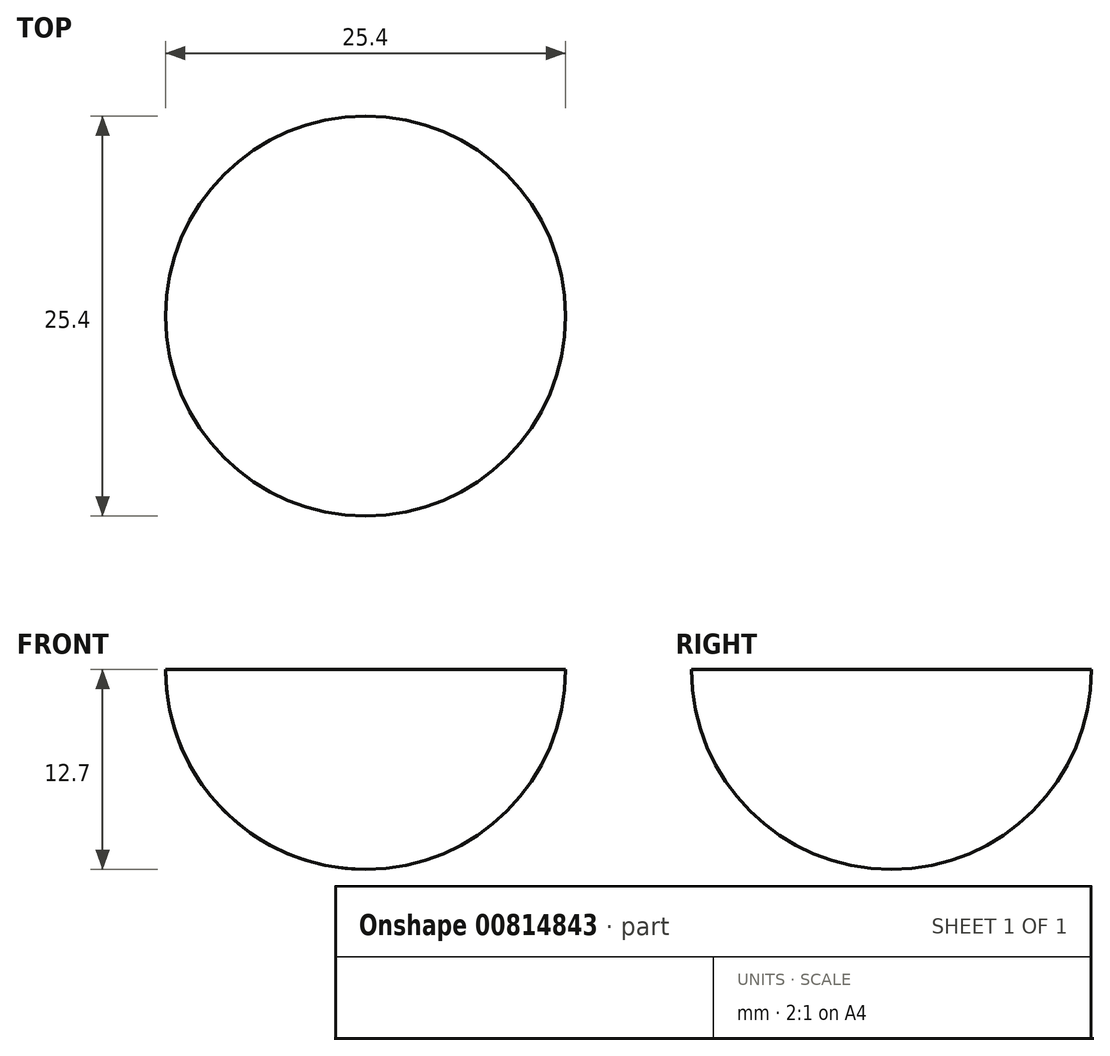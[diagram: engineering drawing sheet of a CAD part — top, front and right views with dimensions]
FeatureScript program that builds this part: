
annotation { "Feature Type Name" : "Feature", "Feature Type Description" : "" }
export const myFeature = defineFeature(function(context is Context, id is Id, definition is map)
    precondition{}
    {
        {
            var Q0;
            Q0=qCreatedBy(makeId("Front.planeOp"),FACE);
            var sketch = newSketch(context, id + "F0", { "sketchPlane" : qUnion([Q0])});
            skArc(sketch, "E0", {"start": v(0, -12.7) * mm, "mid": v(12.7, 0) * mm, "end": v(0, 12.7) * mm});
            skLineSegment(sketch, "E1", {"start": v(0, -12.7) * mm, "end": v(0, 12.7) * mm});
            skSolve(sketch);
        }
        {
            var Q0;
            Q0 = qSketchRegion(id + "F0", true);
            var Q1;
            Q1=sQuery(id+"F0.wireOp",EDGE,"E1");
            revolve(context, id + "F1", {"surfaceOperationType" : NewSurfaceOperationType.NEW, "entities" : qUnion([Q0]), "axis" : qUnion([Q1]), "revolveType" : RevolveType.FULL});
        }
        {
            var Q0;
            Q0=qCreatedBy(makeId("Front.planeOp"),FACE);
            var sketch = newSketch(context, id + "F2", { "sketchPlane" : qUnion([Q0])});
            skLineSegment(sketch, "E2.bottom", {"start": v(-16.12, 0) * mm, "end": v(17.62, 0) * mm});
            skLineSegment(sketch, "E2.top", {"start": v(-16.12, 14.98) * mm, "end": v(17.62, 14.98) * mm});
            skLineSegment(sketch, "E2.left", {"start": v(-16.12, 0) * mm, "end": v(-16.12, 14.98) * mm});
            skLineSegment(sketch, "E2.right", {"start": v(17.62, 0) * mm, "end": v(17.62, 14.98) * mm});
            skSolve(sketch);
        }
        {
            var Q0;
            Q0=makeQuery(id+"F2.imprint","IMPRINT",FACE,{"disambiguationData":[TD([[makeQuery(id+"F2.imprint","IMPRINT",EDGE,{"derivedFrom":sQuery(id+"F2.wireOp",EDGE,"E2.bottom")}),1.0]])]});
            extrude(context, id + "F3", {"entities" : qUnion([Q0]), "operationType" : NewBodyOperationType.REMOVE, "endBound" : BoundingType.SYMMETRIC, "oppositeDirection" : true, "depth" : 25.4 * mm, "offsetDistance" : 25.4 * mm});
        }
    });
